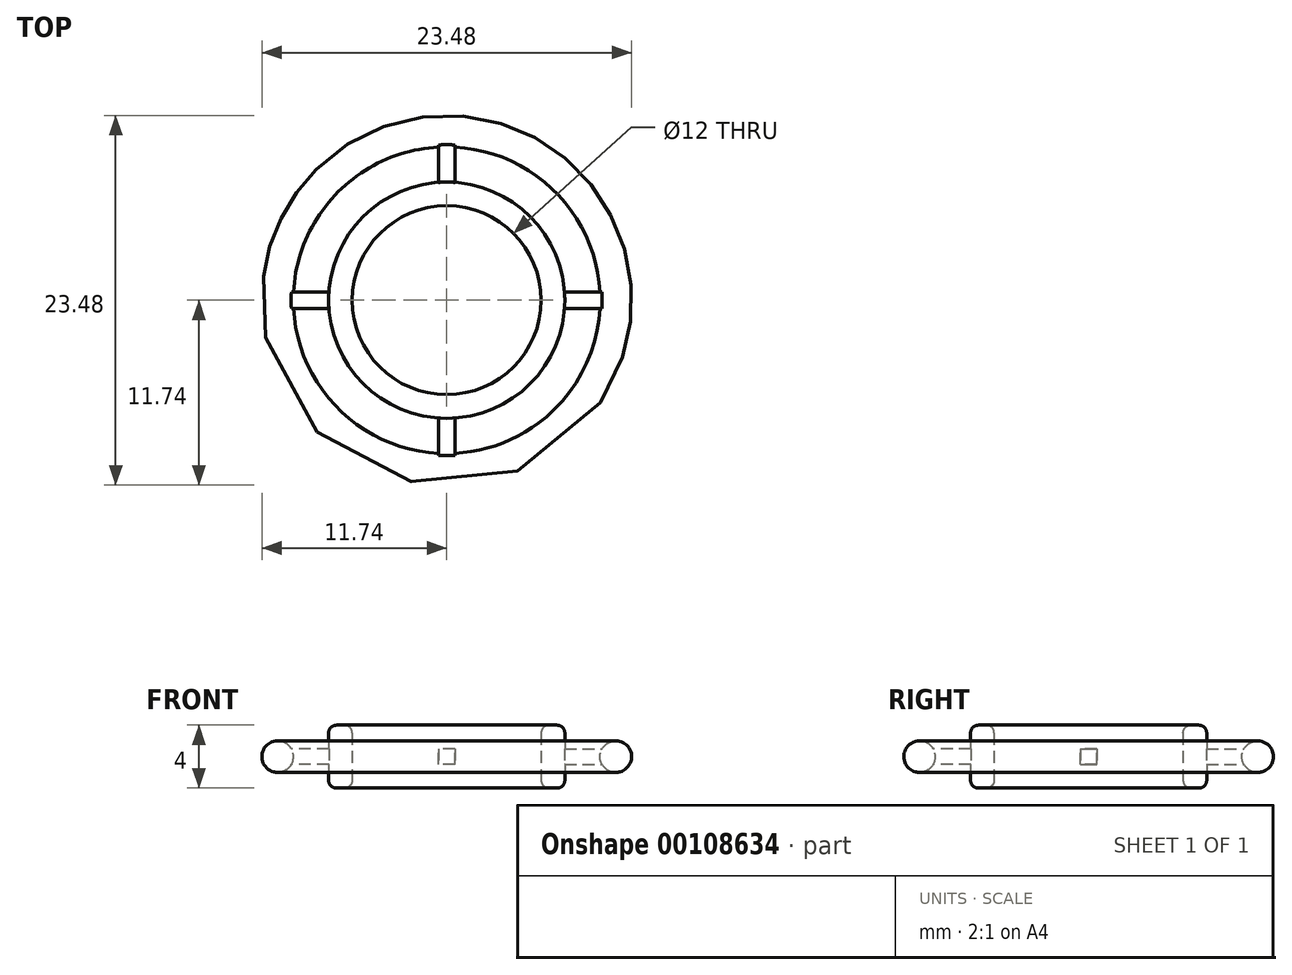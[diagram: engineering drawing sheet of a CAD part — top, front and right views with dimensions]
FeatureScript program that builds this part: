
annotation { "Feature Type Name" : "Feature", "Feature Type Description" : "" }
export const myFeature = defineFeature(function(context is Context, id is Id, definition is map)
    precondition{}
    {
        {
            var Q0;
            Q0=qCreatedBy(makeId("Top.planeOp"),FACE);
            var sketch = newSketch(context, id + "F0", { "sketchPlane" : qUnion([Q0])});
            skCircle(sketch, "E0", {"center": v(0, 0) * mm, "radius": 7.5 * mm});
            skPoint(sketch, "E1", {"position": v(-4.26, 9.97) * mm});
            skPoint(sketch, "E2.MirrorP", {"position": v(4.26, 9.97) * mm});
            skLineSegment(sketch, "E3", {"start": v(-0.52, 0.52) * mm, "end": v(-0.52, 10.03) * mm});
            skLineSegment(sketch, "E4", {"start": v(-0.52, 10.03) * mm, "end": v(0, 10.03) * mm});
            skLineSegment(sketch, "E5", {"start": v(-0.52, 0.52) * mm, "end": v(-10.03, 0.52) * mm});
            skLineSegment(sketch, "E6", {"start": v(-10.03, 0.52) * mm, "end": v(-10.03, 0) * mm});
            skLineSegment(sketch, "E7.MirrorCS", {"start": v(0.52, 10.03) * mm, "end": v(0, 10.03) * mm});
            skLineSegment(sketch, "E8.MirrorCS", {"start": v(0.52, 0.52) * mm, "end": v(0.52, 10.03) * mm});
            skLineSegment(sketch, "E9.MirrorCS", {"start": v(0.52, 0.52) * mm, "end": v(10.03, 0.52) * mm});
            skLineSegment(sketch, "E10.MirrorCS", {"start": v(10.03, 0.52) * mm, "end": v(10.03, 0) * mm});
            skLineSegment(sketch, "E11.MirrorCS", {"start": v(-0.52, -0.52) * mm, "end": v(-0.52, -10.03) * mm});
            skLineSegment(sketch, "E12.MirrorCS", {"start": v(10.03, -0.52) * mm, "end": v(10.03, 0) * mm});
            skLineSegment(sketch, "E13.MirrorCS", {"start": v(0.52, -0.52) * mm, "end": v(0.52, -10.03) * mm});
            skLineSegment(sketch, "E14.MirrorCS", {"start": v(-0.52, -0.52) * mm, "end": v(-10.03, -0.52) * mm});
            skLineSegment(sketch, "E15.MirrorCS", {"start": v(0.52, -0.52) * mm, "end": v(10.03, -0.52) * mm});
            skCircle(sketch, "E16.MirrorC", {"center": v(0, 0) * mm, "radius": 6 * mm});
            skLineSegment(sketch, "E17.MirrorCS", {"start": v(0.52, -10.03) * mm, "end": v(0, -10.03) * mm});
            skLineSegment(sketch, "E18.MirrorCS", {"start": v(-10.03, -0.52) * mm, "end": v(-10.03, 0) * mm});
            skLineSegment(sketch, "E19.MirrorCS", {"start": v(-0.52, -10.03) * mm, "end": v(0, -10.03) * mm});
            skSolve(sketch);
        }
        {
            var Q0;
            {var subQ0=sQuery(id+"F0.wireOp",EDGE,"E0");var subQ1=sQuery(id+"F0.wireOp",EDGE,"E3");var subQ2=makeQuery(id+"F0.imprint","INTERSECT",VERTEX,{"derivedFrom":[subQ1,subQ0]});Q0=makeQuery(id+"F0.imprint","IMPRINT",FACE,{"disambiguationData":[TD([[makeQuery(id+"F0.imprint","IMPRINT",EDGE,{"disambiguationData":[TD([[subQ2,1.0]])],"derivedFrom":subQ1}),1.0]])]});}
            var Q1;
            {var subQ0=sQuery(id+"F0.wireOp",EDGE,"E0");var subQ1=sQuery(id+"F0.wireOp",EDGE,"E8.MirrorCS");var subQ2=makeQuery(id+"F0.imprint","INTERSECT",VERTEX,{"derivedFrom":[subQ1,subQ0]});Q1=makeQuery(id+"F0.imprint","IMPRINT",FACE,{"disambiguationData":[TD([[makeQuery(id+"F0.imprint","IMPRINT",EDGE,{"disambiguationData":[TD([[subQ2,1.0]])],"derivedFrom":subQ1}),-1.0]])]});}
            var Q2;
            {var subQ0=sQuery(id+"F0.wireOp",EDGE,"E0");var subQ1=sQuery(id+"F0.wireOp",EDGE,"E11.MirrorCS");var subQ2=makeQuery(id+"F0.imprint","INTERSECT",VERTEX,{"derivedFrom":[subQ1,subQ0]});Q2=makeQuery(id+"F0.imprint","IMPRINT",FACE,{"disambiguationData":[TD([[makeQuery(id+"F0.imprint","IMPRINT",EDGE,{"disambiguationData":[TD([[subQ2,1.0]])],"derivedFrom":subQ1}),-1.0]])]});}
            var Q3;
            {var subQ0=sQuery(id+"F0.wireOp",EDGE,"E0");var subQ1=sQuery(id+"F0.wireOp",EDGE,"E13.MirrorCS");var subQ2=makeQuery(id+"F0.imprint","INTERSECT",VERTEX,{"derivedFrom":[subQ1,subQ0]});Q3=makeQuery(id+"F0.imprint","IMPRINT",FACE,{"disambiguationData":[TD([[makeQuery(id+"F0.imprint","IMPRINT",EDGE,{"disambiguationData":[TD([[subQ2,1.0]])],"derivedFrom":subQ1}),1.0]])]});}
            var Q4;
            {var subQ0=sQuery(id+"F0.wireOp",EDGE,"E0");var subQ1=sQuery(id+"F0.wireOp",EDGE,"E3");var subQ2=makeQuery(id+"F0.imprint","INTERSECT",VERTEX,{"derivedFrom":[subQ1,subQ0]});Q4=makeQuery(id+"F0.imprint","IMPRINT",FACE,{"disambiguationData":[TD([[makeQuery(id+"F0.imprint","IMPRINT",EDGE,{"disambiguationData":[TD([[subQ2,1.0]])],"derivedFrom":subQ1}),-1.0]])]});}
            var Q5;
            {var subQ0=sQuery(id+"F0.wireOp",EDGE,"E0");var subQ1=sQuery(id+"F0.wireOp",EDGE,"E5");var subQ2=makeQuery(id+"F0.imprint","INTERSECT",VERTEX,{"derivedFrom":[subQ1,subQ0]});Q5=makeQuery(id+"F0.imprint","IMPRINT",FACE,{"disambiguationData":[TD([[makeQuery(id+"F0.imprint","IMPRINT",EDGE,{"disambiguationData":[TD([[subQ2,1.0]])],"derivedFrom":subQ1}),1.0]])]});}
            var Q6;
            {var subQ0=sQuery(id+"F0.wireOp",EDGE,"E0");var subQ1=sQuery(id+"F0.wireOp",EDGE,"E9.MirrorCS");var subQ2=makeQuery(id+"F0.imprint","INTERSECT",VERTEX,{"derivedFrom":[subQ1,subQ0]});Q6=makeQuery(id+"F0.imprint","IMPRINT",FACE,{"disambiguationData":[TD([[makeQuery(id+"F0.imprint","IMPRINT",EDGE,{"disambiguationData":[TD([[subQ2,1.0]])],"derivedFrom":subQ1}),-1.0]])]});}
            var Q7;
            {var subQ0=sQuery(id+"F0.wireOp",EDGE,"E0");var subQ1=sQuery(id+"F0.wireOp",EDGE,"E11.MirrorCS");var subQ2=makeQuery(id+"F0.imprint","INTERSECT",VERTEX,{"derivedFrom":[subQ1,subQ0]});Q7=makeQuery(id+"F0.imprint","IMPRINT",FACE,{"disambiguationData":[TD([[makeQuery(id+"F0.imprint","IMPRINT",EDGE,{"disambiguationData":[TD([[subQ2,1.0]])],"derivedFrom":subQ1}),1.0]])]});}
            extrude(context, id + "F1", {"entities" : qUnion([Q0, Q1, Q2, Q3, Q4, Q5, Q6, Q7]), "endBound" : BoundingType.SYMMETRIC, "depth" : 4 * mm});
        }
        {
            var Q0;
            Q0=makeQuery(id+"F1.opExtrude","CAP_FACE",FACE,{"disambiguationData":[OSD([sQuery(id+"F0.wireOp",EDGE,"E0"),sQuery(id+"F0.wireOp",EDGE,"E16.MirrorC")])],"isStart":false});
            var Q1;
            Q1=makeQuery(id+"F1.opExtrude","CAP_FACE",FACE,{"disambiguationData":[OSD([sQuery(id+"F0.wireOp",EDGE,"E0"),sQuery(id+"F0.wireOp",EDGE,"E16.MirrorC")])],"isStart":true});
            fillet(context, id + "F2", {"entities" : qUnion([Q0, Q1]), "radius" : 0.5 * mm, "tangentPropagation" : true, "allowEdgeOverflow" : false});
        }
        {
            var Q0;
            Q0=qCreatedBy(makeId("Right.planeOp"),FACE);
            var sketch = newSketch(context, id + "F3", { "sketchPlane" : qUnion([Q0])});
            skCircle(sketch, "E20", {"center": v(10.74, 0) * mm, "radius": 1 * mm});
            skLineSegment(sketch, "E21", {"start": v(0, 5.11) * mm, "end": v(0, -5.66) * mm});
            skSolve(sketch);
        }
        {
            var Q0;
            Q0 = qSketchRegion(id + "F3", true);
            var Q1;
            Q1=sQuery(id+"F3.wireOp",EDGE,"E21");
            revolve(context, id + "F4", {"entities" : qUnion([Q0]), "axis" : qUnion([Q1]), "revolveType" : RevolveType.FULL});
        }
        {
            var Q0;
            {var subQ4=sQuery(id+"F0.wireOp",EDGE,"E4");Q0=makeQuery(id+"F0.imprint","IMPRINT",FACE,{"disambiguationData":[TD([[makeQuery(id+"F0.imprint","IMPRINT",EDGE,{"derivedFrom":subQ4}),-1.0]])]});}
            var Q1;
            {var subQ4=sQuery(id+"F0.wireOp",EDGE,"E10.MirrorCS");Q1=makeQuery(id+"F0.imprint","IMPRINT",FACE,{"disambiguationData":[TD([[makeQuery(id+"F0.imprint","IMPRINT",EDGE,{"derivedFrom":subQ4}),-1.0]])]});}
            var Q2;
            {var subQ6=sQuery(id+"F0.wireOp",EDGE,"E17.MirrorCS");Q2=makeQuery(id+"F0.imprint","IMPRINT",FACE,{"disambiguationData":[TD([[makeQuery(id+"F0.imprint","IMPRINT",EDGE,{"derivedFrom":subQ6}),-1.0]])]});}
            var Q3;
            {var subQ4=sQuery(id+"F0.wireOp",EDGE,"E6");Q3=makeQuery(id+"F0.imprint","IMPRINT",FACE,{"disambiguationData":[TD([[makeQuery(id+"F0.imprint","IMPRINT",EDGE,{"derivedFrom":subQ4}),1.0]])]});}
            extrude(context, id + "F5", {"entities" : qUnion([Q0, Q1, Q2, Q3]), "operationType" : NewBodyOperationType.ADD, "endBound" : BoundingType.SYMMETRIC, "depth" : 1 * mm});
        }
    });
